# Revit family: P191568KX-061c_KCES550H
name_source: partatom
category: Specialty Equipment
units: mm (PartAtom-declared; Revit-internal decimal feet)

## family parameters
Always vertical = Yes
Cut with Voids When Loaded = No
Enable Cutting in Views = No
Maintain Annotation Orientation = No
Part Type = Normal
Room Calculation Point = No
Round Connector Dimension = Use Diameter
Shared = No
Work Plane-Based = No

## types (2) — shared parameters
Amps = 0 A
Body Material = ARCAT - Metal - Steel - Stainless
Cooktop Material = ARCAT - Glass - Black
Default Elevation = 0"
Depth = 21 3/4"
Description = 30" Electric Cooktop with 5 Elements and Knob Controls
Table de cuisson électrique à 5 éléments, boutons de commande, 30 po
Family Name = COOKING
Feature 1 = 10'' Even-Heat™ Ultra Power™ Element with Simmer Setting
10'' Even-Heat™ Ultra Power™ Element with Simmer Setting
Feature 2 = 6'' Even-Heat™ Element with Melt Setting
Élément Even-Heat™ avec fonction de fonte, 6 po
Feature 3 = 10''/6'' Ultra Power™ Double-Ring Round Element
Éléments ronds à anneau double Ultra Power™, 10 po/6 po
Height = 5 1/4"
Installation-Fabrication = https://www.whirlpool.com
https://www.whirlpool.com
Knob Material = ARCAT - Metal - Steel - Gray
Manufacturer = KitchenAid
Voltage = 0 V
Width = 30 13/16"

## per-type parameters (varying)
| type | Accent Material | KICU509XBL | KICU509XSS |
| KCES550HSS | ARCAT - Metal - Steel - Gray | No | Yes |
| KCES550HBL | ARCAT - Metal - Steel - Black | Yes | No |

note: column(s) folded — value = type name in every type: Model

## geometry (parser evidence)
native form markers: Sweep x4
no freeform markers — native parametric forms only
